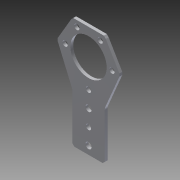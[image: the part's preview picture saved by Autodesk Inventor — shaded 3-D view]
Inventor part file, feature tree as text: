
AUTODESK INVENTOR PART (.ipt)
format: ipt  version: 2014 (Build 180170000, 170)  size: 163,328 bytes
history: native  units: in
note: dims shown in document units (in); Inventor stores cm internally (conversion verified against a paired STEP export)
features: other x2, sketch x1, imported_body x1
ambient origin geometry x8: Origin, YZ Plane, XZ Plane, XY Plane, X Axis, Y Axis, Z Axis, Center Point
bodies: Body1 (feature_tree)
feature tree (4):
  other  "Cut-Extrude1"
  other  "217-3554-STEP1"
  sketch  "Sketch1"  dims[d0=0.19in]
  imported_body  "Base1"
